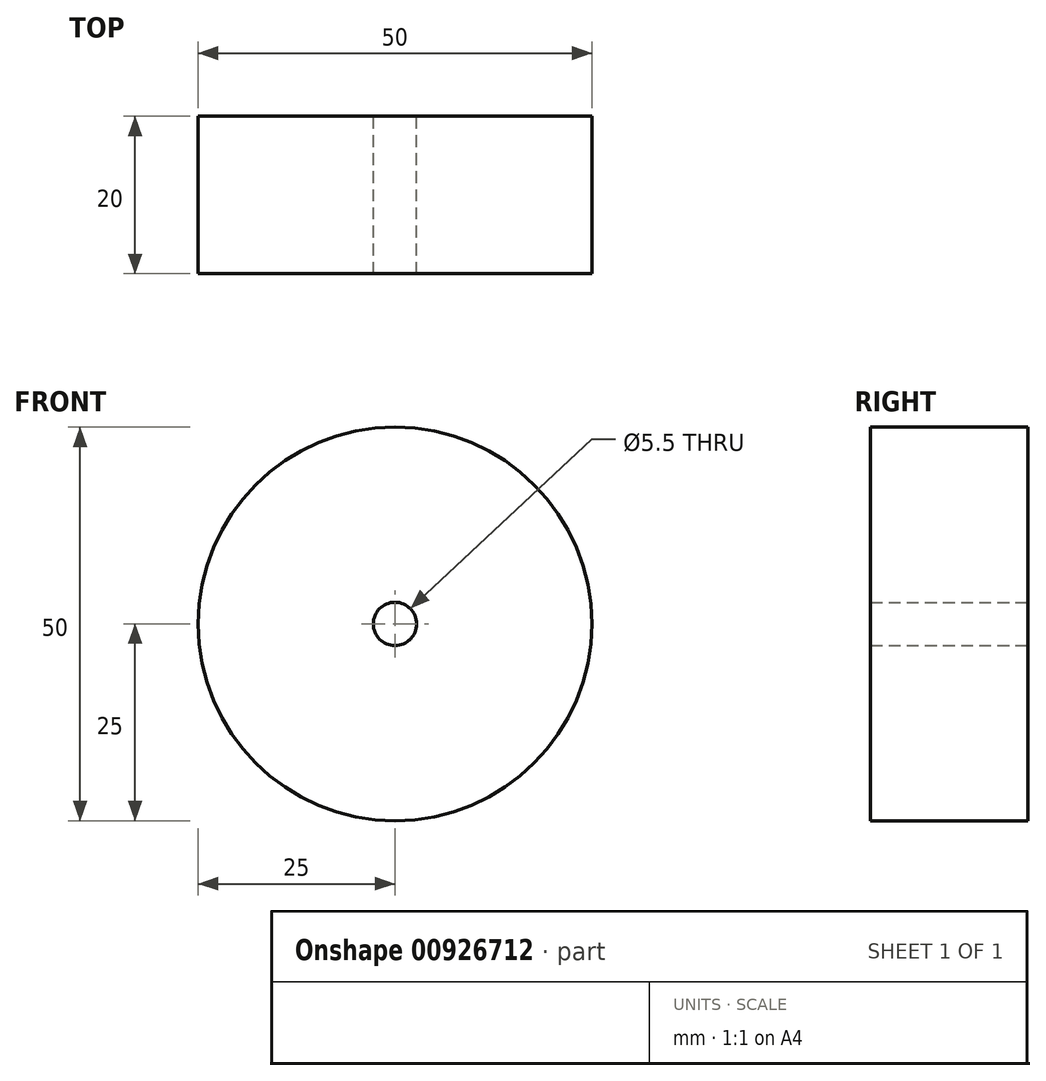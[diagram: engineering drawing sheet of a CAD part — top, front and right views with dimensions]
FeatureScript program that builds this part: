
annotation { "Feature Type Name" : "Feature", "Feature Type Description" : "" }
export const myFeature = defineFeature(function(context is Context, id is Id, definition is map)
    precondition{}
    {
        {
            var Q0;
            Q0=qCreatedBy(makeId("Front.planeOp"),FACE);
            var sketch = newSketch(context, id + "F0", { "sketchPlane" : qUnion([Q0])});
            skCircle(sketch, "E0", {"center": v(0, 0) * mm, "radius": 25 * mm});
            skCircle(sketch, "E1", {"center": v(0, 0) * mm, "radius": 2.75 * mm});
            skSolve(sketch);
        }
        {
            var Q0;
            Q0 = qSketchRegion(id + "F0", true);
            extrude(context, id + "F1", {"entities" : qUnion([Q0]), "depth" : 20 * mm, "offsetDistance" : 25 * mm});
        }
    });
